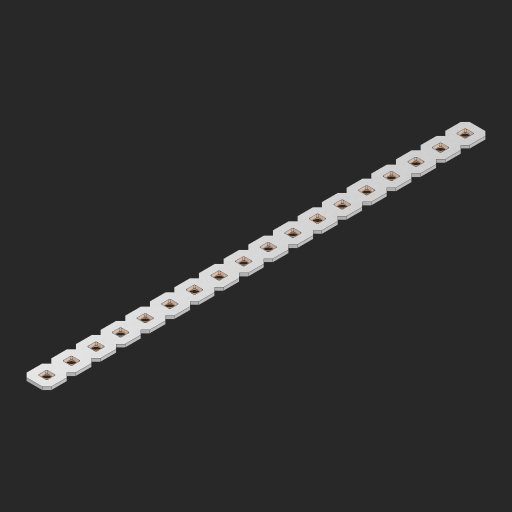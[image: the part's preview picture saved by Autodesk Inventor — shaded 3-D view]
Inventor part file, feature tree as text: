
AUTODESK INVENTOR PART (.ipt)
format: ipt  version: 2023 (Build 270158000, 158)  size: 465,920 bytes
history: native  units: in
note: dims shown in document units (in); Inventor stores cm internally (conversion verified against a paired STEP export)
features: other x19, extrude x17, sketch x2, pattern_linear x1
ambient origin geometry x8: Origin, YZ Plane, XZ Plane, XY Plane, X Axis, Y Axis, Z Axis, Center Point
bodies: Solid1 (feature_tree), Body (feature_tree)
feature tree (39):
  pattern_linear  "Rectangular Pattern1"  Spacing1=0.09in  [1 undecoded]
  sketch  "Sketch1"  dims[d1=0.5in]
  sketch  "Sketch2"  dims[d2=0.182in d3=0.09in d4=0.09in d5=0.09in d6=0.09in d7=0.09in d8=0.09in d9=0.09in d10=0.09in d11=0.02in d13=0.0in d14=0.172in d15=0.0625in d16=0.0in d19=0.5in d22=0.5in]
  other  "Srf1"
  other  "Srf126"
  other  "Srf127"
  other  "Srf128"
  other  "Srf129"
  other  "Srf130"
  other  "Srf131"
  other  "Srf250"
  other  "Srf251"
  other  "Srf252"
  other  "Srf253"
  other  "Srf254"
  other  "Srf255"
  other  "Srf256"
  other  "Srf257"
  other  "Srf258"
  other  "Srf259"
  other  "Srf260"
  other  "Circle"
  extrude  "ExtrusionSrf126"  Depth=0.09in
  extrude  "ExtrusionSrf127"  Depth=0.09in
  extrude  "ExtrusionSrf128"  Depth=0.09in
  extrude  "ExtrusionSrf129"  Depth=0.09in
  extrude  "ExtrusionSrf130"  Depth=0.09in
  extrude  "ExtrusionSrf131"  Depth=0.09in
  extrude  "ExtrusionSrf250"  Depth=0.09in
  extrude  "ExtrusionSrf251"  Depth=0.02in
  extrude  "ExtrusionSrf252"  TaperAngle=0.0deg  [1 undecoded]
  extrude  "ExtrusionSrf253"  Depth=0.5in
  extrude  "ExtrusionSrf254"  Depth=0.0625in TaperAngle=0.0deg
  extrude  "ExtrusionSrf255"  Depth=0.5in
  extrude  "ExtrusionSrf256"  Depth=0.5in
  extrude  "ExtrusionSrf257"  [1 undecoded]
  extrude  "ExtrusionSrf258"  [1 undecoded]
  extrude  "ExtrusionSrf259"  [1 undecoded]
  extrude  "ExtrusionSrf260"  [1 undecoded]
note: 6 required parameter values undecoded (feature->parameter linkage not recoverable at this tier; creation-order binding heuristic only, values carry confidence <= 0.55)
